# Revit family: SANINDUSA_131024004CX_EasyWDCloseCoupledRimFlushToilet_342x625x390_Easy
name_source: partatom
category: Plumbing Fixtures
units: mm (PartAtom-declared; Revit-internal decimal feet)

## family parameters
Cut with Voids When Loaded = No
Host = Face
Part Type = Normal
Room Calculation Point = No
Round Connector Dimension = Use Diameter
Shared = No

## types (1)
- SANINDUSA_131024004CX_EasyWDCloseCoupledRimFlushToilet_342x625x390_Easy
    AssetType = Fixed
    CodePerformance = EN 997:2012+A1:2015    CL 1 - 6 A
    Color = white
    Constituents = Compatible toilet seats (not included): 23131 - Easy toilet seat with slowclose system; 23114 - Easy toilet seat with top fixing hinges; 23121 - Easy thermoplast toilet seat;  Compatible cisterns (not included): 131111LM - Easy bottom water supply connection cistern with dual flush mechanism; 131113LM - Easy side water supply connection cistern with dual flush mechanism; 131141LM - Easy bottom water supply connection cistern with 3/4.5L mechanism; 131143LM - Easy side water supply connection cistern with 3/4.5L mechanism: 42 - fixing kit (included).
    Default Elevation = 1219 mm
    Description = Soil appliance for the disposal of excrement.
    DrainSize = 100 mm  [stored 0.328084 ft]
    Element Type = TOILETPAN: Soil appliance for the disposal of excrement.
    Features = "Domestic and commercial use. Versatile timeless design. Seats easy to clean and slow close option. Back to wall WC. "
    Finish = gloss
    InletDiameter = 0 mm  [stored 0 ft]
    Installation Instructions = https://www.tec.sanindusa.pt
    Manufacturer = Sanindusa
    ManufacturerName = Sanindusa
    ManufacturerURL = www.tec.sanindusa.pt
    Material = vitreous china
    Model = 131024004CX
    ModelNumber = 131024004CX
    ModelReference = Easy
    Name = Easy W|D close coupled rimflush toilet
    NominalHeight = 390 mm  [stored 1.27953 ft]
    NominalLength = 342 mm  [stored 1.12205 ft]
    NominalWidth = 625 mm  [stored 2.05052 ft]
    PanColor = white
    PanMaterial = vitreous china
    PanMounting = pedestal
    Pre-defined type (IFC) = TOILETPAN
    ProductInformation = https://www.tec.sanindusa.pt
    ProductionYear = 2021
    Size = 342x625x390
    ToiletPanType = washdown
    ToiletType = LooseCoupled
    Type (IFC) = IfcSanitaryTerminalType
    URL = www.tec.sanindusa.pt
    Version = 1
    WarrantyDescription = https://www.tec.sanindusa.pt
    WarrantyDurationParts = 5
    WarrantyDurationUnit = year
    Waste Connection = Yes
    Weight = 22.50 kg

note: [stored X ft] marks values corroborated as IEEE doubles in the binary element streams (Revit-internal decimal feet)

## geometry (parser evidence)
native form markers: Sweep x5
no freeform markers — native parametric forms only
